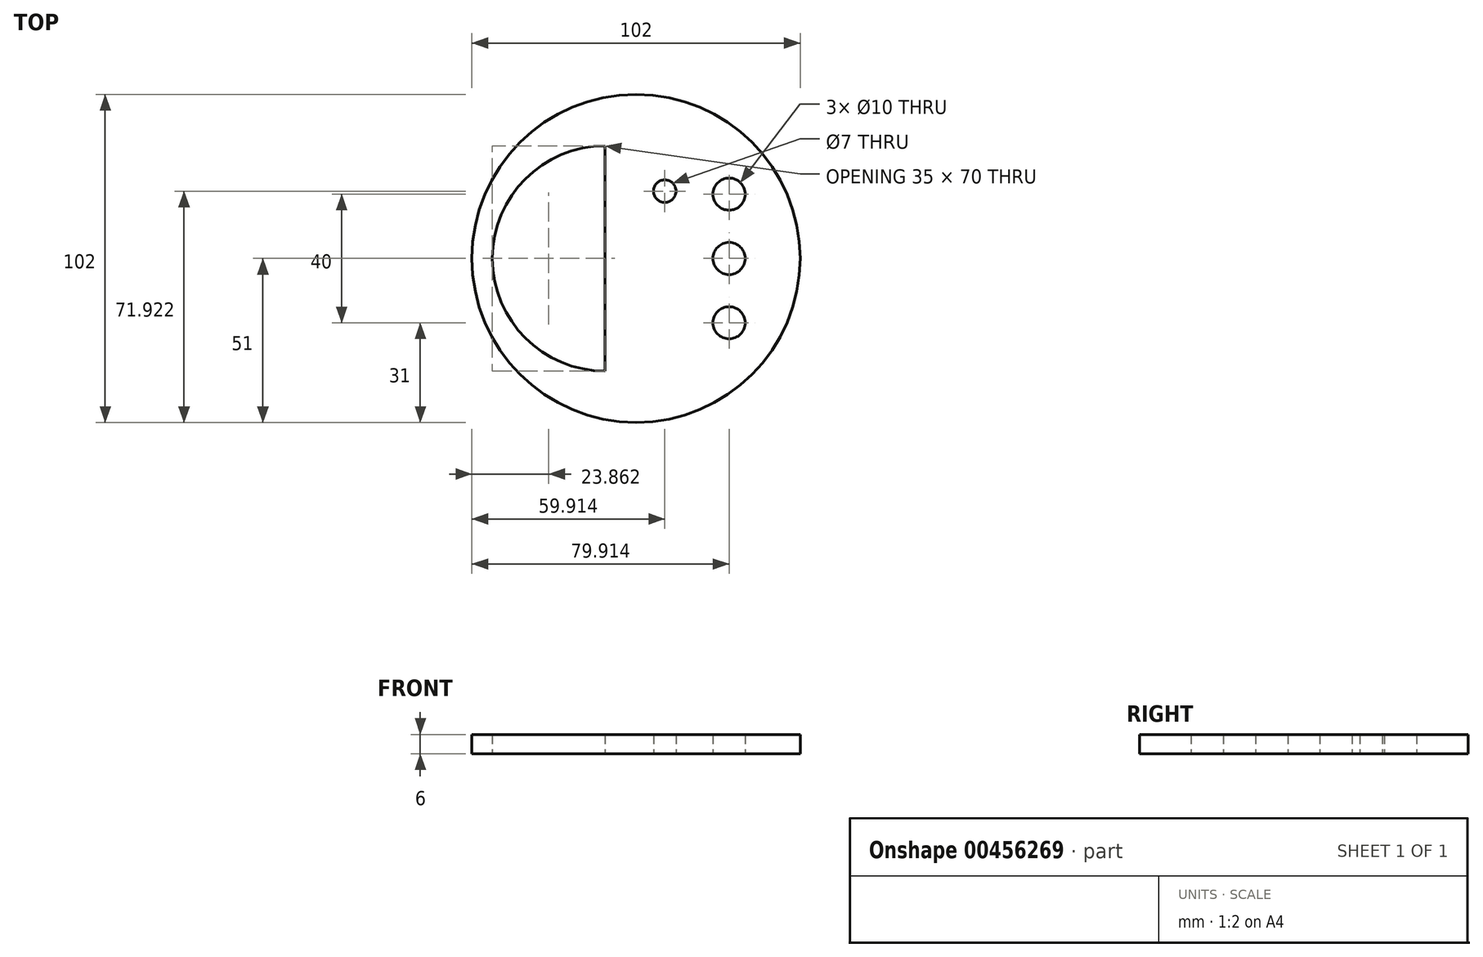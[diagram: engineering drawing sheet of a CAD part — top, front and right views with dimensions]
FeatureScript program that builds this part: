
annotation { "Feature Type Name" : "Feature", "Feature Type Description" : "" }
export const myFeature = defineFeature(function(context is Context, id is Id, definition is map)
    precondition{}
    {
        {
            var Q0;
            Q0=qCreatedBy(makeId("Top.planeOp"),FACE);
            var sketch = newSketch(context, id + "F0", { "sketchPlane" : qUnion([Q0])});
            skCircle(sketch, "E0", {"center": v(0, 0) * mm, "radius": 51 * mm});
            skCircle(sketch, "E1", {"center": v(28.91, 20) * mm, "radius": 5 * mm});
            skCircle(sketch, "E2", {"center": v(28.91, 0) * mm, "radius": 5 * mm});
            skCircle(sketch, "E3", {"center": v(28.91, -20) * mm, "radius": 5 * mm});
            skLineSegment(sketch, "E4", {"start": v(-9.64, 35) * mm, "end": v(-9.64, -35) * mm});
            skPoint(sketch, "E5.startSnap0", {"position": v(-9.64, 0) * mm});
            skArc(sketch, "E6", {"start": v(-44.64, 0) * mm, "mid": v(-34.39, -24.75) * mm, "end": v(-9.64, -35) * mm});
            skArc(sketch, "E7", {"start": v(-44.64, 0) * mm, "mid": v(-34.39, 24.75) * mm, "end": v(-9.64, 35) * mm});
            skCircle(sketch, "E8", {"center": v(8.91, 20.92) * mm, "radius": 3.5 * mm});
            skSolve(sketch);
        }
        {
            var Q0;
            Q0=makeQuery(id+"F0.imprint","IMPRINT",FACE,{"disambiguationData":[TD([[makeQuery(id+"F0.imprint","IMPRINT",EDGE,{"derivedFrom":sQuery(id+"F0.wireOp",EDGE,"E0")}),1.0]])]});
            extrude(context, id + "F1", {"entities" : qUnion([Q0]), "depth" : 6 * mm});
        }
    });
